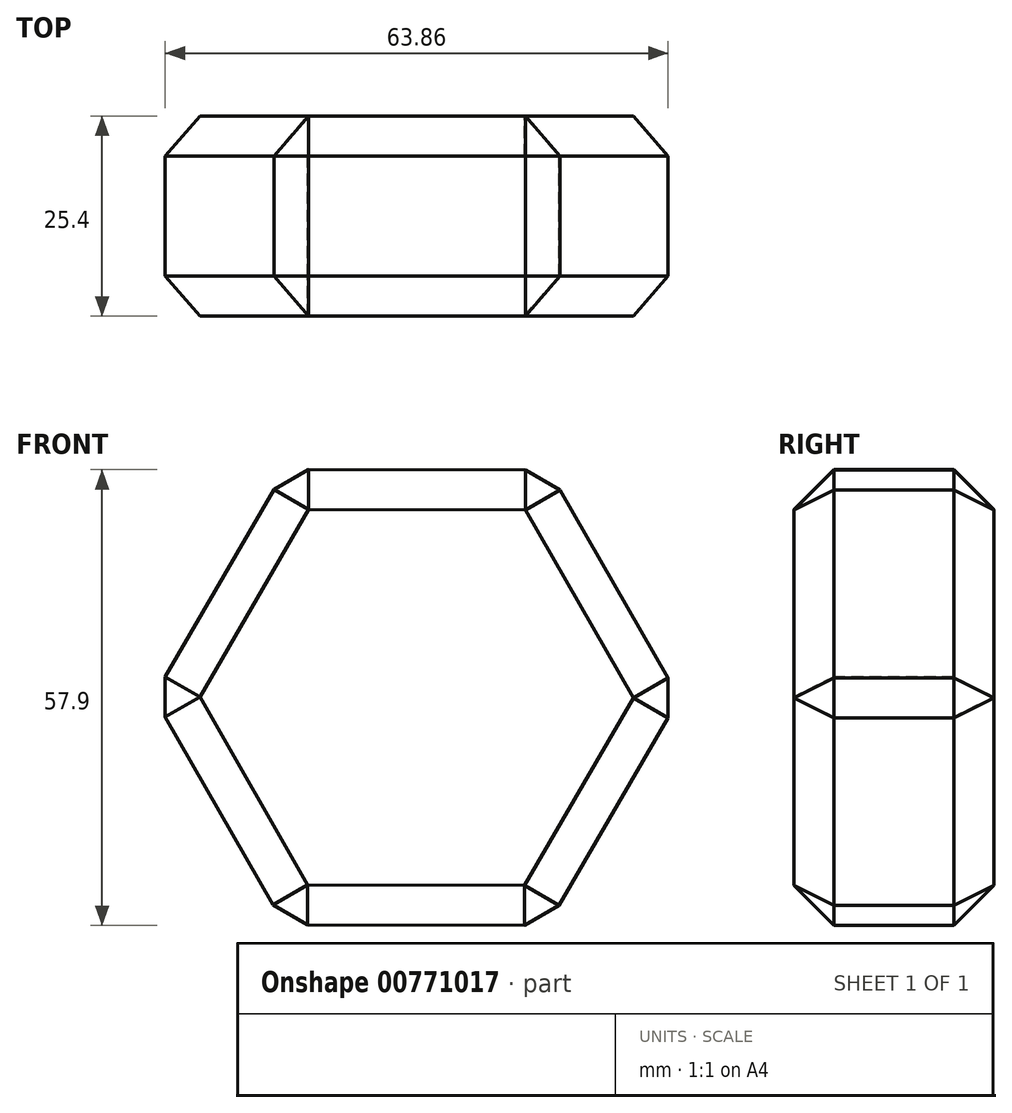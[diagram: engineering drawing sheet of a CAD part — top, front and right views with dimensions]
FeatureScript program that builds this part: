
annotation { "Feature Type Name" : "Feature", "Feature Type Description" : "" }
export const myFeature = defineFeature(function(context is Context, id is Id, definition is map)
    precondition{}
    {
        {
            var Q0;
            Q0=qCreatedBy(makeId("Front.planeOp"),FACE);
            var sketch = newSketch(context, id + "F0", { "sketchPlane" : qUnion([Q0])});
            skCircle(sketch, "E0.cCircle", {"center": v(0, 0) * mm, "radius": 33.4 * mm, "construction": true});
            skLineSegment(sketch, "E0.0", {"start": v(-16.63, 28.96) * mm, "end": v(16.76, 28.88) * mm});
            skLineSegment(sketch, "E0.1", {"start": v(16.76, 28.88) * mm, "end": v(33.4, -0.08) * mm});
            skLineSegment(sketch, "E0.2", {"start": v(33.4, -0.08) * mm, "end": v(16.63, -28.96) * mm});
            skLineSegment(sketch, "E0.3", {"start": v(16.63, -28.96) * mm, "end": v(-16.76, -28.88) * mm});
            skLineSegment(sketch, "E0.4", {"start": v(-16.76, -28.88) * mm, "end": v(-33.4, 0.08) * mm});
            skLineSegment(sketch, "E0.5", {"start": v(-33.4, 0.08) * mm, "end": v(-16.63, 28.96) * mm});
            skSolve(sketch);
        }
        {
            var Q0;
            Q0=makeQuery(id+"F0.imprint","IMPRINT",FACE,{"disambiguationData":[TD([[makeQuery(id+"F0.imprint","IMPRINT",EDGE,{"derivedFrom":sQuery(id+"F0.wireOp",EDGE,"E0.0")}),-1.0]])]});
            extrude(context, id + "F1", {"entities" : qUnion([Q0]), "endBound" : BoundingType.SYMMETRIC, "depth" : 25.4 * mm, "offsetDistance" : 25.4 * mm});
        }
        {
            var Q0;
            Q0=makeQuery(id+"F1.opExtrude","SWEPT_FACE",FACE,{"disambiguationData":[OSD([sQuery(id+"F0.wireOp",EDGE,"E0.1")])]});
            var Q1;
            Q1=makeQuery(id+"F1.opExtrude","SWEPT_FACE",FACE,{"disambiguationData":[OSD([sQuery(id+"F0.wireOp",EDGE,"E0.0")])]});
            var Q2;
            Q2=makeQuery(id+"F1.opExtrude","SWEPT_FACE",FACE,{"disambiguationData":[OSD([sQuery(id+"F0.wireOp",EDGE,"E0.2")])]});
            var Q3;
            Q3=makeQuery(id+"F1.opExtrude","SWEPT_FACE",FACE,{"disambiguationData":[OSD([sQuery(id+"F0.wireOp",EDGE,"E0.3")])]});
            var Q4;
            Q4=makeQuery(id+"F1.opExtrude","CAP_EDGE",EDGE,{"disambiguationData":[OSD([sQuery(id+"F0.wireOp",EDGE,"E0.4")])],"isStart":false});
            var Q5;
            Q5=makeQuery(id+"F1.opExtrude","SWEPT_FACE",FACE,{"disambiguationData":[OSD([sQuery(id+"F0.wireOp",EDGE,"E0.4")])]});
            var Q6;
            Q6=makeQuery(id+"F1.opExtrude","CAP_EDGE",EDGE,{"disambiguationData":[OSD([sQuery(id+"F0.wireOp",EDGE,"E0.5")])],"isStart":true});
            var Q7;
            Q7=makeQuery(id+"F1.opExtrude","CAP_EDGE",EDGE,{"disambiguationData":[OSD([sQuery(id+"F0.wireOp",EDGE,"E0.5")])],"isStart":false});
            chamfer(context, id + "F2", {"entities" : qUnion([Q0, Q1, Q2, Q3, Q4, Q5, Q6, Q7]), "width" : 5.08 * mm, "tangentPropagation" : true});
        }
    });
